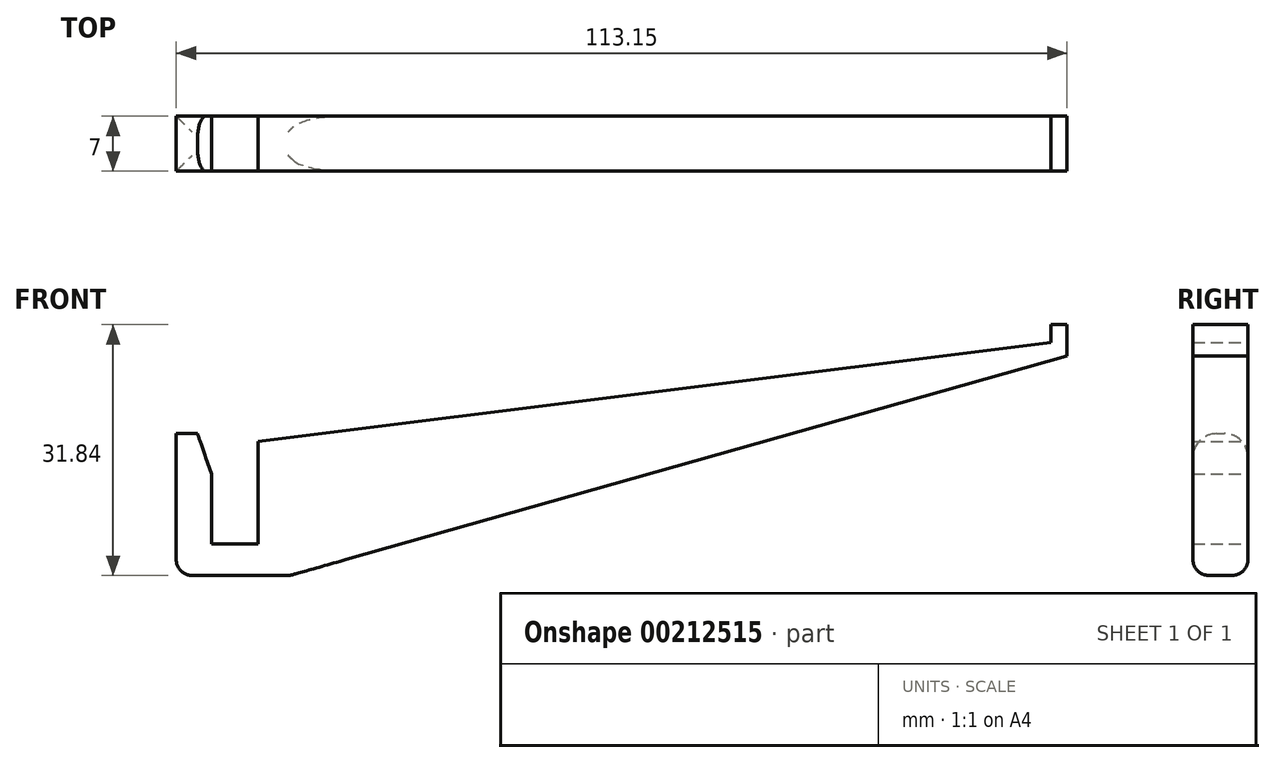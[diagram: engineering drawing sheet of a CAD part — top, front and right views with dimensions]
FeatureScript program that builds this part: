
annotation { "Feature Type Name" : "Feature", "Feature Type Description" : "" }
export const myFeature = defineFeature(function(context is Context, id is Id, definition is map)
    precondition{}
    {
        {
            var Q0;
            Q0=qCreatedBy(makeId("Front.planeOp"),FACE);
            var sketch = newSketch(context, id + "F0", { "sketchPlane" : qUnion([Q0])});
            skLineSegment(sketch, "E0", {"start": v(-34.14, -10.76) * mm, "end": v(-34.14, -1.9) * mm});
            skLineSegment(sketch, "E1", {"start": v(-38.64, -1.76) * mm, "end": v(-38.64, -14.76) * mm});
            skLineSegment(sketch, "E2", {"start": v(-38.64, -14.76) * mm, "end": v(-24.14, -14.76) * mm});
            skLineSegment(sketch, "E3", {"start": v(-28.24, -1.76) * mm, "end": v(-28.24, -10.76) * mm});
            skLineSegment(sketch, "E4", {"start": v(-28.24, -10.76) * mm, "end": v(-34.14, -10.76) * mm});
            skLineSegment(sketch, "E5", {"start": v(-37.74, 3.24) * mm, "end": v(-35.94, 3.24) * mm});
            skLineSegment(sketch, "E6", {"start": v(-38.64, -1.76) * mm, "end": v(-38.64, 3.24) * mm});
            skLineSegment(sketch, "E7", {"start": v(-37.74, 3.24) * mm, "end": v(-38.64, 3.24) * mm});
            skLineSegment(sketch, "E8", {"start": v(-28.24, -1.76) * mm, "end": v(-28.24, 2.24) * mm});
            skLineSegment(sketch, "E9", {"start": v(-28.24, 2.24) * mm, "end": v(72.5, 14.83) * mm});
            skLineSegment(sketch, "E10", {"start": v(74.5, 15.08) * mm, "end": v(74.5, 13.08) * mm});
            skLineSegment(sketch, "E11", {"start": v(74.5, 15.08) * mm, "end": v(74.5, 17.08) * mm});
            skLineSegment(sketch, "E12", {"start": v(74.5, 17.08) * mm, "end": v(72.5, 17.08) * mm});
            skLineSegment(sketch, "E13", {"start": v(72.5, 17.08) * mm, "end": v(72.5, 14.83) * mm});
            skLineSegment(sketch, "E14", {"start": v(-24.14, -14.76) * mm, "end": v(74.5, 13.08) * mm});
            skLineSegment(sketch, "E15", {"start": v(-35.94, 3.24) * mm, "end": v(-34.14, -1.9) * mm});
            skPoint(sketch, "E16.orphan", {"position": v(-34.14, 3.24) * mm});
            skSolve(sketch);
        }
        {
            var Q0;
            Q0=makeQuery(id+"F0.imprint","IMPRINT",FACE,{"disambiguationData":[TD([[makeQuery(id+"F0.imprint","IMPRINT",EDGE,{"derivedFrom":sQuery(id+"F0.wireOp",EDGE,"E0")}),1.0]])]});
            extrude(context, id + "F1", {"entities" : qUnion([Q0]), "endBound" : BoundingType.SYMMETRIC, "depth" : 7 * mm});
        }
        {
            var Q0;
            Q0=makeQuery(id+"F1.opExtrude","CAP_EDGE",EDGE,{"disambiguationData":[OSD([sQuery(id+"F0.wireOp",EDGE,"E5"),sQuery(id+"F0.wireOp",EDGE,"E7")])],"isStart":true});
            var Q1;
            Q1=makeQuery(id+"F1.opExtrude","CAP_EDGE",EDGE,{"disambiguationData":[OSD([sQuery(id+"F0.wireOp",EDGE,"E5"),sQuery(id+"F0.wireOp",EDGE,"E7")])],"isStart":false});
            fillet(context, id + "F2", {"entities" : qUnion([Q0, Q1]), "radius" : 3 * mm, "tangentPropagation" : true, "allowEdgeOverflow" : false});
        }
        {
            var Q0;
            Q0=makeQuery(id+"F1.opExtrude","SWEPT_FACE",FACE,{"disambiguationData":[OSD([sQuery(id+"F0.wireOp",EDGE,"E2")])]});
            var Q1;
            Q1=makeQuery(id+"F2.opFillet","BLEND_EDGE",EDGE,{"blendedFrom":[makeQuery(id+"F1.opExtrude","CAP_EDGE",EDGE,{"disambiguationData":[OSD([sQuery(id+"F0.wireOp",EDGE,"E5"),sQuery(id+"F0.wireOp",EDGE,"E7")])],"isStart":true}),makeQuery(id+"F1.opExtrude","SWEPT_FACE",FACE,{"disambiguationData":[OSD([sQuery(id+"F0.wireOp",EDGE,"E0")])]})],"blendedInto":[makeQuery(id+"F1.opExtrude","SWEPT_FACE",FACE,{"disambiguationData":[OSD([sQuery(id+"F0.wireOp",EDGE,"E0")])]})]});
            fillet(context, id + "F3", {"entities" : qUnion([Q0, Q1]), "radius" : 2 * mm, "tangentPropagation" : true, "allowEdgeOverflow" : false});
        }
    });
